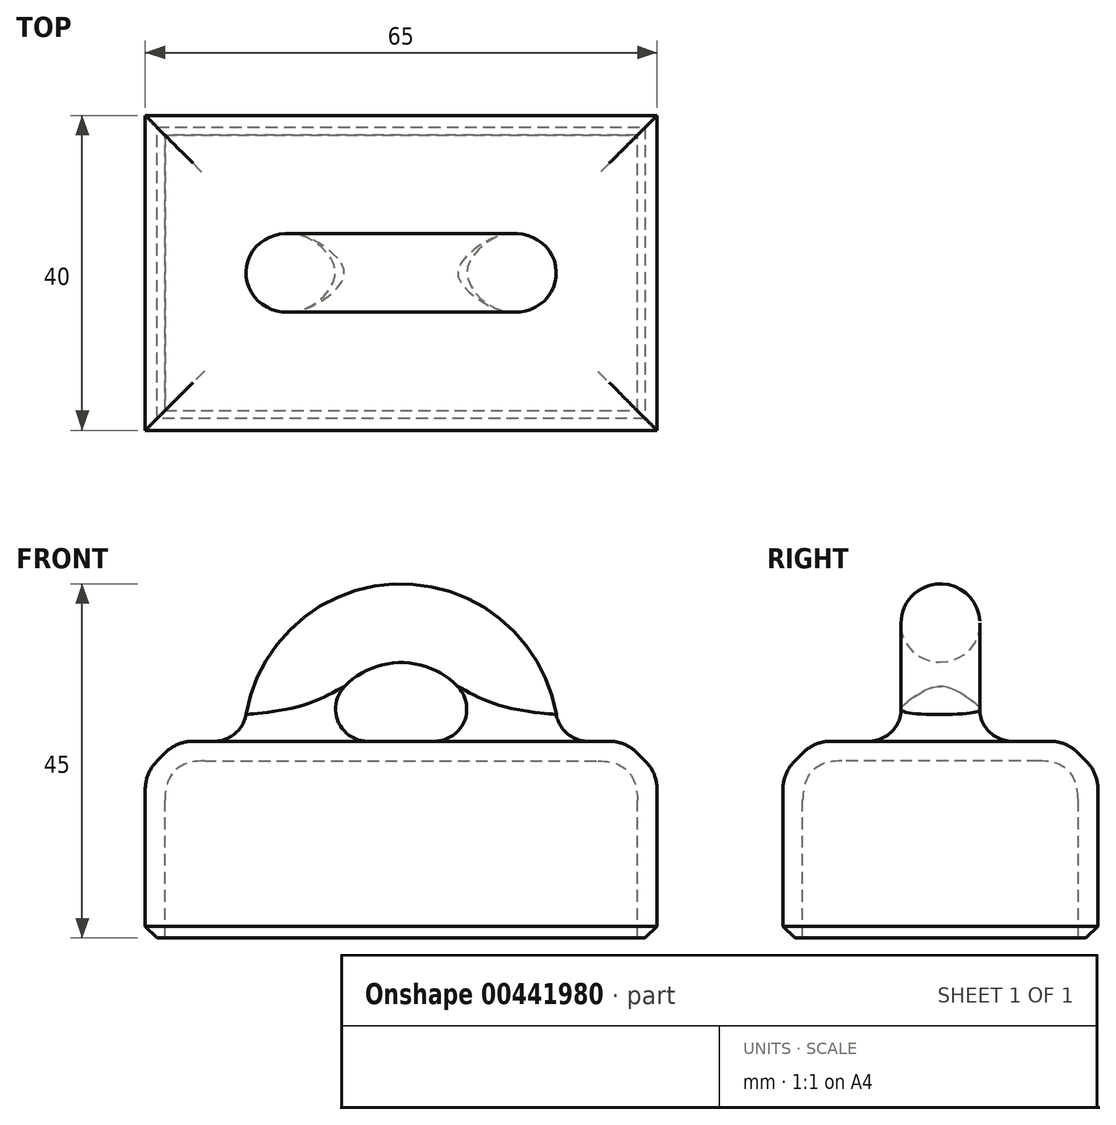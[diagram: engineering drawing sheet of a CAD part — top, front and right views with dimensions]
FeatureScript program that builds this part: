
annotation { "Feature Type Name" : "Feature", "Feature Type Description" : "" }
export const myFeature = defineFeature(function(context is Context, id is Id, definition is map)
    precondition{}
    {
        {
            var Q0;
            Q0=qCreatedBy(makeId("Top.planeOp"),FACE);
            var sketch = newSketch(context, id + "F0", { "sketchPlane" : qUnion([Q0])});
            skLineSegment(sketch, "E0.bottom", {"start": v(-23.34, 49.03) * mm, "end": v(41.66, 49.03) * mm});
            skLineSegment(sketch, "E0.top", {"start": v(-23.34, 9.03) * mm, "end": v(41.66, 9.03) * mm});
            skLineSegment(sketch, "E0.left", {"start": v(-23.34, 49.03) * mm, "end": v(-23.34, 9.03) * mm});
            skLineSegment(sketch, "E0.right", {"start": v(41.66, 49.03) * mm, "end": v(41.66, 9.03) * mm});
            skSolve(sketch);
        }
        {
            var Q0;
            Q0=qSketchRegion(id+"F0",true);
            extrude(context, id + "F1", {"entities" : qUnion([Q0]), "depth" : 25 * mm});
        }
        {
            var Q0;
            Q0=makeQuery(id+"F1.opExtrude","CAP_FACE",FACE,{"disambiguationData":[OSD([sQuery(id+"F0.wireOp",EDGE,"E0.bottom"),sQuery(id+"F0.wireOp",EDGE,"E0.top"),sQuery(id+"F0.wireOp",EDGE,"E0.left"),sQuery(id+"F0.wireOp",EDGE,"E0.right")])],"isStart":false});
            shell(context, id + "F2", {"entities" : qUnion([Q0]), "thickness" : 2.5 * mm});
        }
        {
            var Q0;
            {var subQ0=sQuery(id+"F0.wireOp",EDGE,"E0.left");Q0=makeQuery(id+"F2.opShell","OFFSET_EDGE",EDGE,{"disambiguationData":[OSD([subQ0]),TDD([makeQuery(id+"F1.opExtrude","CAP_EDGE",EDGE,{"disambiguationData":[OSD([subQ0])],"isStart":true})])]});}
            var Q1;
            {var subQ0=sQuery(id+"F0.wireOp",EDGE,"E0.top");Q1=makeQuery(id+"F2.opShell","OFFSET_EDGE",EDGE,{"disambiguationData":[OSD([subQ0]),TDD([makeQuery(id+"F1.opExtrude","CAP_EDGE",EDGE,{"disambiguationData":[OSD([subQ0])],"isStart":true})])]});}
            var Q2;
            {var subQ0=sQuery(id+"F0.wireOp",EDGE,"E0.bottom");Q2=makeQuery(id+"F2.opShell","OFFSET_EDGE",EDGE,{"disambiguationData":[OSD([subQ0]),TDD([makeQuery(id+"F1.opExtrude","CAP_EDGE",EDGE,{"disambiguationData":[OSD([subQ0])],"isStart":true})])]});}
            var Q3;
            {var subQ0=sQuery(id+"F0.wireOp",EDGE,"E0.right");Q3=makeQuery(id+"F2.opShell","OFFSET_EDGE",EDGE,{"disambiguationData":[OSD([subQ0]),TDD([makeQuery(id+"F1.opExtrude","CAP_EDGE",EDGE,{"disambiguationData":[OSD([subQ0])],"isStart":true})])]});}
            fillet(context, id + "F3", {"entities" : qUnion([Q0, Q1, Q2, Q3]), "radius" : 5 * mm, "tangentPropagation" : true, "rho" : 0.5, "crossSection" : FilletCrossSection.CONIC, "allowEdgeOverflow" : false});
        }
        {
            var Q0;
            Q0=makeQuery(id+"F1.opExtrude","CAP_EDGE",EDGE,{"disambiguationData":[OSD([sQuery(id+"F0.wireOp",EDGE,"E0.top")])],"isStart":true});
            var Q1;
            Q1=makeQuery(id+"F1.opExtrude","CAP_EDGE",EDGE,{"disambiguationData":[OSD([sQuery(id+"F0.wireOp",EDGE,"E0.left")])],"isStart":true});
            var Q2;
            Q2=makeQuery(id+"F1.opExtrude","CAP_EDGE",EDGE,{"disambiguationData":[OSD([sQuery(id+"F0.wireOp",EDGE,"E0.bottom")])],"isStart":true});
            var Q3;
            Q3=makeQuery(id+"F1.opExtrude","CAP_EDGE",EDGE,{"disambiguationData":[OSD([sQuery(id+"F0.wireOp",EDGE,"E0.right")])],"isStart":true});
            chamfer(context, id + "F4", {"entities" : qUnion([Q0, Q1, Q2, Q3]), "width" : 4 * mm, "tangentPropagation" : true});
        }
        {
            var Q0;
            Q0=makeQuery(id+"F1.opExtrude","SWEPT_BODY",BODY,{"disambiguationData":[OSD([sQuery(id+"F0.wireOp",EDGE,"E0.bottom"),sQuery(id+"F0.wireOp",EDGE,"E0.top"),sQuery(id+"F0.wireOp",EDGE,"E0.left"),sQuery(id+"F0.wireOp",EDGE,"E0.right")])]});
            transform(context, id + "F5", {"entities" : qUnion([Q0]), "transformType" : TransformType.TRANSLATION_3D, "dx" : 0 * mm, "dy" : 0 * mm, "dz" : 26.3 * mm, "makeCopy" : false});
        }
        {
            var Q0;
            Q0=makeQuery(id+"F1.opExtrude","SWEPT_BODY",BODY,{"disambiguationData":[OSD([sQuery(id+"F0.wireOp",EDGE,"E0.bottom"),sQuery(id+"F0.wireOp",EDGE,"E0.top"),sQuery(id+"F0.wireOp",EDGE,"E0.left"),sQuery(id+"F0.wireOp",EDGE,"E0.right")])]});
            var Q1;
            {var subQ0=sQuery(id+"F0.wireOp",EDGE,"E0.bottom");Q1=makeQuery(id+"F4.opChamfer","BLEND_EDGE",EDGE,{"blendedFrom":[makeQuery(id+"F1.opExtrude","CAP_EDGE",EDGE,{"disambiguationData":[OSD([subQ0])],"isStart":true}),makeQuery(id+"F1.opExtrude","CAP_FACE",FACE,{"disambiguationData":[OSD([subQ0,sQuery(id+"F0.wireOp",EDGE,"E0.top"),sQuery(id+"F0.wireOp",EDGE,"E0.left"),sQuery(id+"F0.wireOp",EDGE,"E0.right")])],"isStart":true})],"blendedInto":[makeQuery(id+"F1.opExtrude","CAP_FACE",FACE,{"disambiguationData":[OSD([subQ0,sQuery(id+"F0.wireOp",EDGE,"E0.top"),sQuery(id+"F0.wireOp",EDGE,"E0.left"),sQuery(id+"F0.wireOp",EDGE,"E0.right")])],"isStart":true})]});}
            transform(context, id + "F6", {"entities" : qUnion([Q0]), "transformType" : TransformType.ROTATION, "transformAxis" : qUnion([Q1]), "angle" : 180 * degree, "makeCopy" : false});
        }
        {
            var Q0;
            Q0=makeQuery(id+"F1.opExtrude","SWEPT_BODY",BODY,{"disambiguationData":[OSD([sQuery(id+"F0.wireOp",EDGE,"E0.bottom"),sQuery(id+"F0.wireOp",EDGE,"E0.top"),sQuery(id+"F0.wireOp",EDGE,"E0.left"),sQuery(id+"F0.wireOp",EDGE,"E0.right")])]});
            transform(context, id + "F7", {"entities" : qUnion([Q0]), "transformType" : TransformType.TRANSLATION_3D, "dx" : 0 * mm, "dy" : -25.1 * mm, "dz" : -1.2 * mm, "makeCopy" : false});
        }
        {
            var Q0;
            Q0=makeQuery(id+"F1.opExtrude","CAP_FACE",FACE,{"disambiguationData":[OSD([sQuery(id+"F0.wireOp",EDGE,"E0.bottom"),sQuery(id+"F0.wireOp",EDGE,"E0.top"),sQuery(id+"F0.wireOp",EDGE,"E0.left"),sQuery(id+"F0.wireOp",EDGE,"E0.right")])],"isStart":true});
            var sketch = newSketch(context, id + "F8", { "sketchPlane" : qUnion([Q0])});
            skCircle(sketch, "E1", {"center": v(-5.84, 35.93) * mm, "radius": 5 * mm});
            skCircle(sketch, "E2", {"center": v(24.16, 35.93) * mm, "radius": 5 * mm});
            skLineSegment(sketch, "E3", {"start": v(9.16, 51.93) * mm, "end": v(9.16, 19.93) * mm});
            skPoint(sketch, "E3.endSnap0", {"position": v(9.16, 19.93) * mm});
            skSolve(sketch);
        }
        {
            var Q0;
            Q0=qSketchRegion(id+"F8",true);
            var Q1;
            Q1=sQuery(id+"F8.wireOp",EDGE,"E3");
            revolve(context, id + "F9", {"operationType" : NewBodyOperationType.ADD, "entities" : qUnion([Q0]), "axis" : qUnion([Q1]), "revolveType" : RevolveType.TWO_DIRECTIONS, "angle" : 120 * degree, "angleBack" : 270 * degree});
        }
        {
            var Q0;
            Q0=makeQuery(id+"F1.opExtrude","CAP_FACE",FACE,{"disambiguationData":[OSD([sQuery(id+"F0.wireOp",EDGE,"E0.bottom"),sQuery(id+"F0.wireOp",EDGE,"E0.top"),sQuery(id+"F0.wireOp",EDGE,"E0.left"),sQuery(id+"F0.wireOp",EDGE,"E0.right")])],"isStart":false});
            var sketch = newSketch(context, id + "F10", { "sketchPlane" : qUnion([Q0])});
            skLineSegment(sketch, "E4.bottom", {"start": v(-11.1, -30.71) * mm, "end": v(29.36, -30.71) * mm});
            skLineSegment(sketch, "E4.top", {"start": v(-11.1, -41.73) * mm, "end": v(29.36, -41.73) * mm});
            skLineSegment(sketch, "E4.left", {"start": v(-11.1, -30.71) * mm, "end": v(-11.1, -41.73) * mm});
            skLineSegment(sketch, "E4.right", {"start": v(29.36, -30.71) * mm, "end": v(29.36, -41.73) * mm});
            skSolve(sketch);
        }
        {
            var Q0;
            Q0=makeQuery(id+"F10.imprint","IMPRINT",FACE,{"disambiguationData":[TD([[makeQuery(id+"F10.imprint","IMPRINT",EDGE,{"derivedFrom":sQuery(id+"F10.wireOp",EDGE,"E4.bottom")}),-1.0]])]});
            extrude(context, id + "F11", {"entities" : qUnion([Q0]), "operationType" : NewBodyOperationType.REMOVE, "oppositeDirection" : true, "depth" : 22.5 * mm});
        }
        {
            var Q0;
            {var subQ0=sQuery(id+"F0.wireOp",EDGE,"E0.bottom");Q0=makeQuery(id+"F4.opChamfer","BLEND_EDGE",EDGE,{"blendedFrom":[makeQuery(id+"F1.opExtrude","CAP_EDGE",EDGE,{"disambiguationData":[OSD([subQ0])],"isStart":true}),makeQuery(id+"F1.opExtrude","CAP_FACE",FACE,{"disambiguationData":[OSD([subQ0,sQuery(id+"F0.wireOp",EDGE,"E0.top"),sQuery(id+"F0.wireOp",EDGE,"E0.left"),sQuery(id+"F0.wireOp",EDGE,"E0.right")])],"isStart":true})],"blendedInto":[makeQuery(id+"F1.opExtrude","CAP_FACE",FACE,{"disambiguationData":[OSD([subQ0,sQuery(id+"F0.wireOp",EDGE,"E0.top"),sQuery(id+"F0.wireOp",EDGE,"E0.left"),sQuery(id+"F0.wireOp",EDGE,"E0.right")])],"isStart":true})]});}
            var Q1;
            {var subQ0=sQuery(id+"F0.wireOp",EDGE,"E0.right");Q1=makeQuery(id+"F4.opChamfer","BLEND_EDGE",EDGE,{"blendedFrom":[makeQuery(id+"F1.opExtrude","CAP_EDGE",EDGE,{"disambiguationData":[OSD([subQ0])],"isStart":true}),makeQuery(id+"F1.opExtrude","CAP_FACE",FACE,{"disambiguationData":[OSD([sQuery(id+"F0.wireOp",EDGE,"E0.bottom"),sQuery(id+"F0.wireOp",EDGE,"E0.top"),sQuery(id+"F0.wireOp",EDGE,"E0.left"),subQ0])],"isStart":true})],"blendedInto":[makeQuery(id+"F1.opExtrude","CAP_FACE",FACE,{"disambiguationData":[OSD([sQuery(id+"F0.wireOp",EDGE,"E0.bottom"),sQuery(id+"F0.wireOp",EDGE,"E0.top"),sQuery(id+"F0.wireOp",EDGE,"E0.left"),subQ0])],"isStart":true})]});}
            var Q2;
            {var subQ0=sQuery(id+"F0.wireOp",EDGE,"E0.top");Q2=makeQuery(id+"F4.opChamfer","BLEND_EDGE",EDGE,{"blendedFrom":[makeQuery(id+"F1.opExtrude","CAP_EDGE",EDGE,{"disambiguationData":[OSD([subQ0])],"isStart":true}),makeQuery(id+"F1.opExtrude","CAP_FACE",FACE,{"disambiguationData":[OSD([sQuery(id+"F0.wireOp",EDGE,"E0.bottom"),subQ0,sQuery(id+"F0.wireOp",EDGE,"E0.left"),sQuery(id+"F0.wireOp",EDGE,"E0.right")])],"isStart":true})],"blendedInto":[makeQuery(id+"F1.opExtrude","CAP_FACE",FACE,{"disambiguationData":[OSD([sQuery(id+"F0.wireOp",EDGE,"E0.bottom"),subQ0,sQuery(id+"F0.wireOp",EDGE,"E0.left"),sQuery(id+"F0.wireOp",EDGE,"E0.right")])],"isStart":true})]});}
            var Q3;
            {var subQ0=sQuery(id+"F0.wireOp",EDGE,"E0.left");Q3=makeQuery(id+"F4.opChamfer","BLEND_EDGE",EDGE,{"blendedFrom":[makeQuery(id+"F1.opExtrude","CAP_EDGE",EDGE,{"disambiguationData":[OSD([subQ0])],"isStart":true}),makeQuery(id+"F1.opExtrude","CAP_FACE",FACE,{"disambiguationData":[OSD([sQuery(id+"F0.wireOp",EDGE,"E0.bottom"),sQuery(id+"F0.wireOp",EDGE,"E0.top"),subQ0,sQuery(id+"F0.wireOp",EDGE,"E0.right")])],"isStart":true})],"blendedInto":[makeQuery(id+"F1.opExtrude","CAP_FACE",FACE,{"disambiguationData":[OSD([sQuery(id+"F0.wireOp",EDGE,"E0.bottom"),sQuery(id+"F0.wireOp",EDGE,"E0.top"),subQ0,sQuery(id+"F0.wireOp",EDGE,"E0.right")])],"isStart":true})]});}
            var Q4;
            {var subQ0=sQuery(id+"F0.wireOp",EDGE,"E0.right");Q4=makeQuery(id+"F4.opChamfer","BLEND_EDGE",EDGE,{"blendedFrom":[makeQuery(id+"F1.opExtrude","CAP_EDGE",EDGE,{"disambiguationData":[OSD([subQ0])],"isStart":true}),makeQuery(id+"F1.opExtrude","SWEPT_FACE",FACE,{"disambiguationData":[OSD([subQ0])]})],"blendedInto":[makeQuery(id+"F1.opExtrude","SWEPT_FACE",FACE,{"disambiguationData":[OSD([subQ0])]})]});}
            var Q5;
            {var subQ0=sQuery(id+"F0.wireOp",EDGE,"E0.top");Q5=makeQuery(id+"F4.opChamfer","BLEND_EDGE",EDGE,{"blendedFrom":[makeQuery(id+"F1.opExtrude","CAP_EDGE",EDGE,{"disambiguationData":[OSD([subQ0])],"isStart":true}),makeQuery(id+"F1.opExtrude","SWEPT_FACE",FACE,{"disambiguationData":[OSD([subQ0])]})],"blendedInto":[makeQuery(id+"F1.opExtrude","SWEPT_FACE",FACE,{"disambiguationData":[OSD([subQ0])]})]});}
            var Q6;
            {var subQ0=sQuery(id+"F0.wireOp",EDGE,"E0.left");Q6=makeQuery(id+"F4.opChamfer","BLEND_EDGE",EDGE,{"blendedFrom":[makeQuery(id+"F1.opExtrude","CAP_EDGE",EDGE,{"disambiguationData":[OSD([subQ0])],"isStart":true}),makeQuery(id+"F1.opExtrude","SWEPT_FACE",FACE,{"disambiguationData":[OSD([subQ0])]})],"blendedInto":[makeQuery(id+"F1.opExtrude","SWEPT_FACE",FACE,{"disambiguationData":[OSD([subQ0])]})]});}
            var Q7;
            {var subQ0=sQuery(id+"F0.wireOp",EDGE,"E0.bottom");Q7=makeQuery(id+"F4.opChamfer","BLEND_EDGE",EDGE,{"blendedFrom":[makeQuery(id+"F1.opExtrude","CAP_EDGE",EDGE,{"disambiguationData":[OSD([subQ0])],"isStart":true}),makeQuery(id+"F1.opExtrude","SWEPT_FACE",FACE,{"disambiguationData":[OSD([subQ0])]})],"blendedInto":[makeQuery(id+"F1.opExtrude","SWEPT_FACE",FACE,{"disambiguationData":[OSD([subQ0])]})]});}
            fillet(context, id + "F12", {"entities" : qUnion([Q0, Q1, Q2, Q3, Q4, Q5, Q6, Q7]), "radius" : 5 * mm, "tangentPropagation" : true, "allowEdgeOverflow" : false});
        }
        {
            var Q0;
            Q0=makeQuery(id+"F9.boolean.opBoolean","MERGE",FACE,{"disambiguationData":[OD(1.0)],"derivedFrom":[makeQuery(id+"F9.opRevolve","SWEPT_FACE",FACE,{"disambiguationData":[OSD([sQuery(id+"F8.wireOp",EDGE,"E1")])]}),makeQuery(id+"F9.opRevolve","SWEPT_FACE",FACE,{"disambiguationData":[OSD([sQuery(id+"F8.wireOp",EDGE,"E2")])]})]});
            fillet(context, id + "F13", {"entities" : qUnion([Q0]), "radius" : 4.1 * mm, "tangentPropagation" : true, "allowEdgeOverflow" : false});
        }
        {
            var Q0;
            Q0=makeQuery(id+"F1.opExtrude","CAP_EDGE",EDGE,{"disambiguationData":[OSD([sQuery(id+"F0.wireOp",EDGE,"E0.top")])],"isStart":false});
            var Q1;
            Q1=makeQuery(id+"F1.opExtrude","CAP_EDGE",EDGE,{"disambiguationData":[OSD([sQuery(id+"F0.wireOp",EDGE,"E0.left")])],"isStart":false});
            var Q2;
            Q2=makeQuery(id+"F1.opExtrude","CAP_EDGE",EDGE,{"disambiguationData":[OSD([sQuery(id+"F0.wireOp",EDGE,"E0.right")])],"isStart":false});
            var Q3;
            Q3=makeQuery(id+"F1.opExtrude","CAP_EDGE",EDGE,{"disambiguationData":[OSD([sQuery(id+"F0.wireOp",EDGE,"E0.bottom")])],"isStart":false});
            chamfer(context, id + "F14", {"entities" : qUnion([Q0, Q1, Q2, Q3]), "width" : 1.5 * mm, "tangentPropagation" : true});
        }
    });
